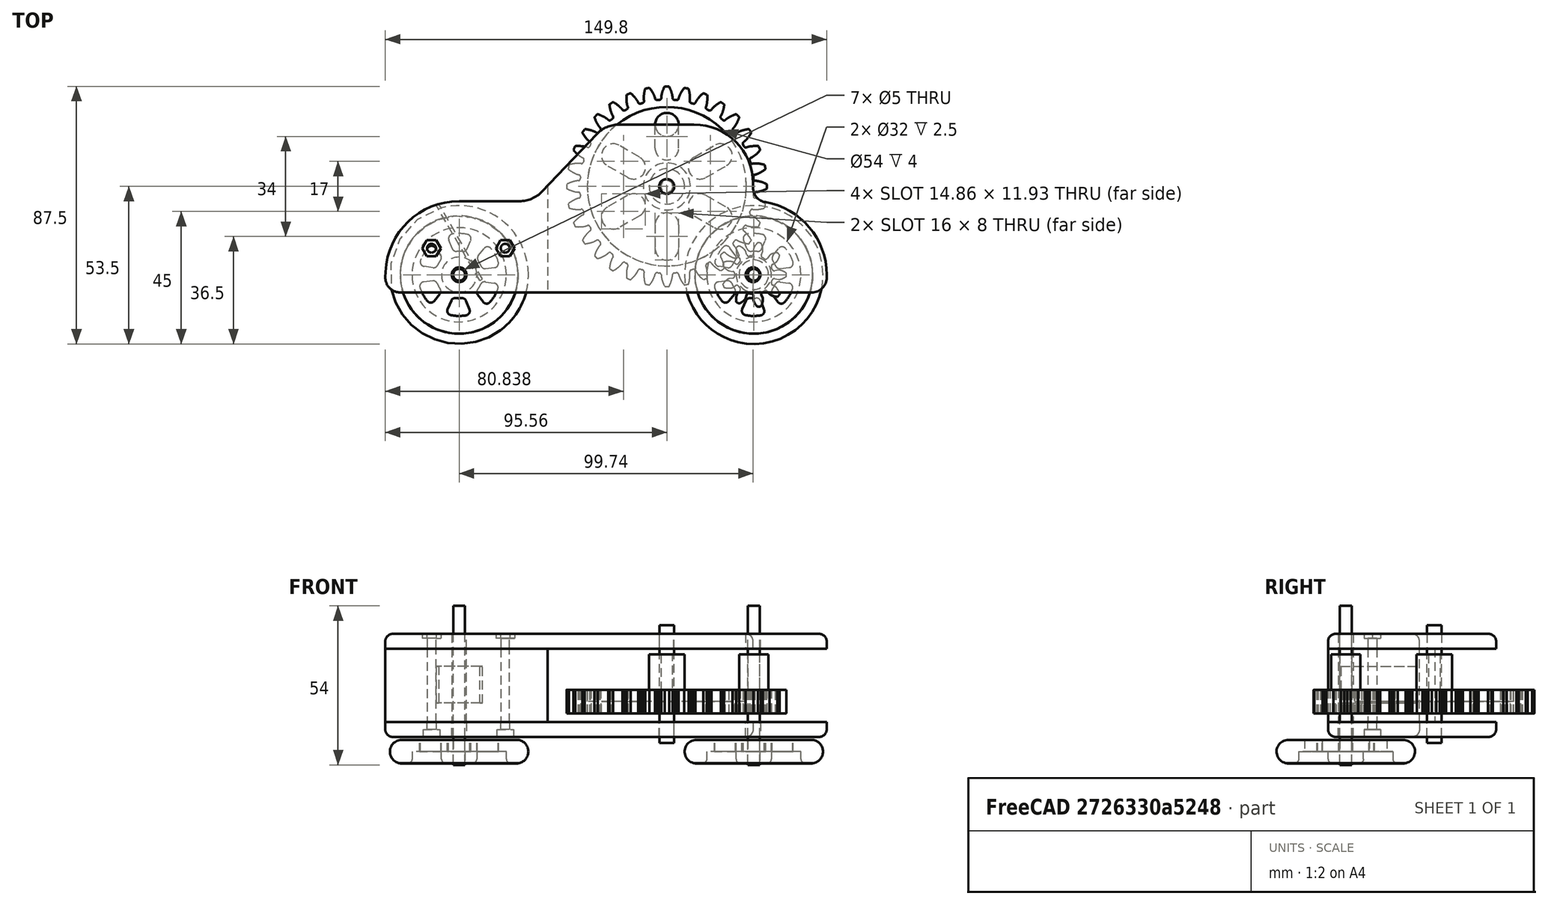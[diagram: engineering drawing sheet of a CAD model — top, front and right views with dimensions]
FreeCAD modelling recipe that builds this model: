
FCSTD DOCUMENT  (FreeCAD 0.14R3700 (Git))
Label: conjunto
License: CC-BY 3.0
LicenseURL: http://creativecommons.org/licenses/by/3.0/
objects: Part::Feature×3, Part::Cylinder×3, PartDesign::Pad×2, Part::Mirroring×2, Part::Cut×1, PartDesign::Fillet×1, App::DocumentObjectGroup×1
note: 14 computed .brp shape members not serialized (recipe doc carries the construction recipe); baked Part::Feature solids carry a one-line shape summary decoded from their .brp

FEATURE [Part::Cut] Cut  label="separador"
FEATURE [PartDesign::Fillet] Fillet  label="tapatornillo"
  Placement = pos=(0,0,0) rot=(0,1,0;3.14159rad)
  Radius = 2.5
FEATURE [Part::Feature] Fillet001  label="tapatuerca"
  Placement = pos=(0,0,25) rot=(0,0,1;0rad)
  shape: bbox 153.8 x 59.06 x 5 mm, 51 faces (baked)
FEATURE [PartDesign::Pad] Pad  label="engragrande"
  Length = 4
  Length2 = 100
  Placement = pos=(70.5,30,3) rot=(0,0,1;0rad)
  Type = 0
FEATURE [PartDesign::Pad] Pad002  label="engranapeque"
  Length = 12
  Length2 = 100
  Placement = pos=(100,0,3) rot=(0,0,1;0rad)
  Type = 0
FEATURE [Part::Cylinder] Cylinder  label="eje1"
  Angle = 360
  Height = 54
  Placement = pos=(0,0,-14.5) rot=(0,0,1;0rad)
  Radius = 2
FEATURE [Part::Cylinder] Cylinder001  label="eje2"
  Angle = 360
  Height = 54
  Placement = pos=(100,0,-14.5) rot=(0,0,1;0rad)
  Radius = 2
FEATURE [Part::Cylinder] Cylinder002  label="eje3"
  Angle = 360
  Height = 40
  Placement = pos=(70.5,30,-7) rot=(0,0,1;0rad)
  Radius = 2.5
FEATURE [Part::Feature] Fusion  label="RuedaA"
  Placement = pos=(0,0,31) rot=(0,0,1;0rad)
  shape: bbox 50.87 x 50.87 x 8 mm, 61 faces (baked)
FEATURE [Part::Feature] Fusion001  label="RuedaB"
  Placement = pos=(100,0,31) rot=(0,0,1;0rad)
  shape: bbox 50.87 x 50.87 x 8 mm, 61 faces (baked)
FEATURE [Part::Mirroring] Part__Mirroring  label="RuedaA1"
  Base = (0,0,0)
  Normal = (0,0,1)
  Placement = pos=(0,0,25) rot=(0,0,1;0rad)
  Source = -> Fusion
FEATURE [Part::Mirroring] Part__Mirroring001  label="RuedaB1"
  Base = (0,0,0)
  Normal = (0,0,1)
  Placement = pos=(0,0,25) rot=(0,0,1;0rad)
  Source = -> Fusion001
FEATURE [App::DocumentObjectGroup] Grupo  label="conjunto"
  Group = -> [Cut,Fillet,Fillet001,Pad002,Pad,Cylinder,Cylinder001,Cylinder002,Fusion,Fusion001,Part__Mirroring,Part__Mirroring001]
